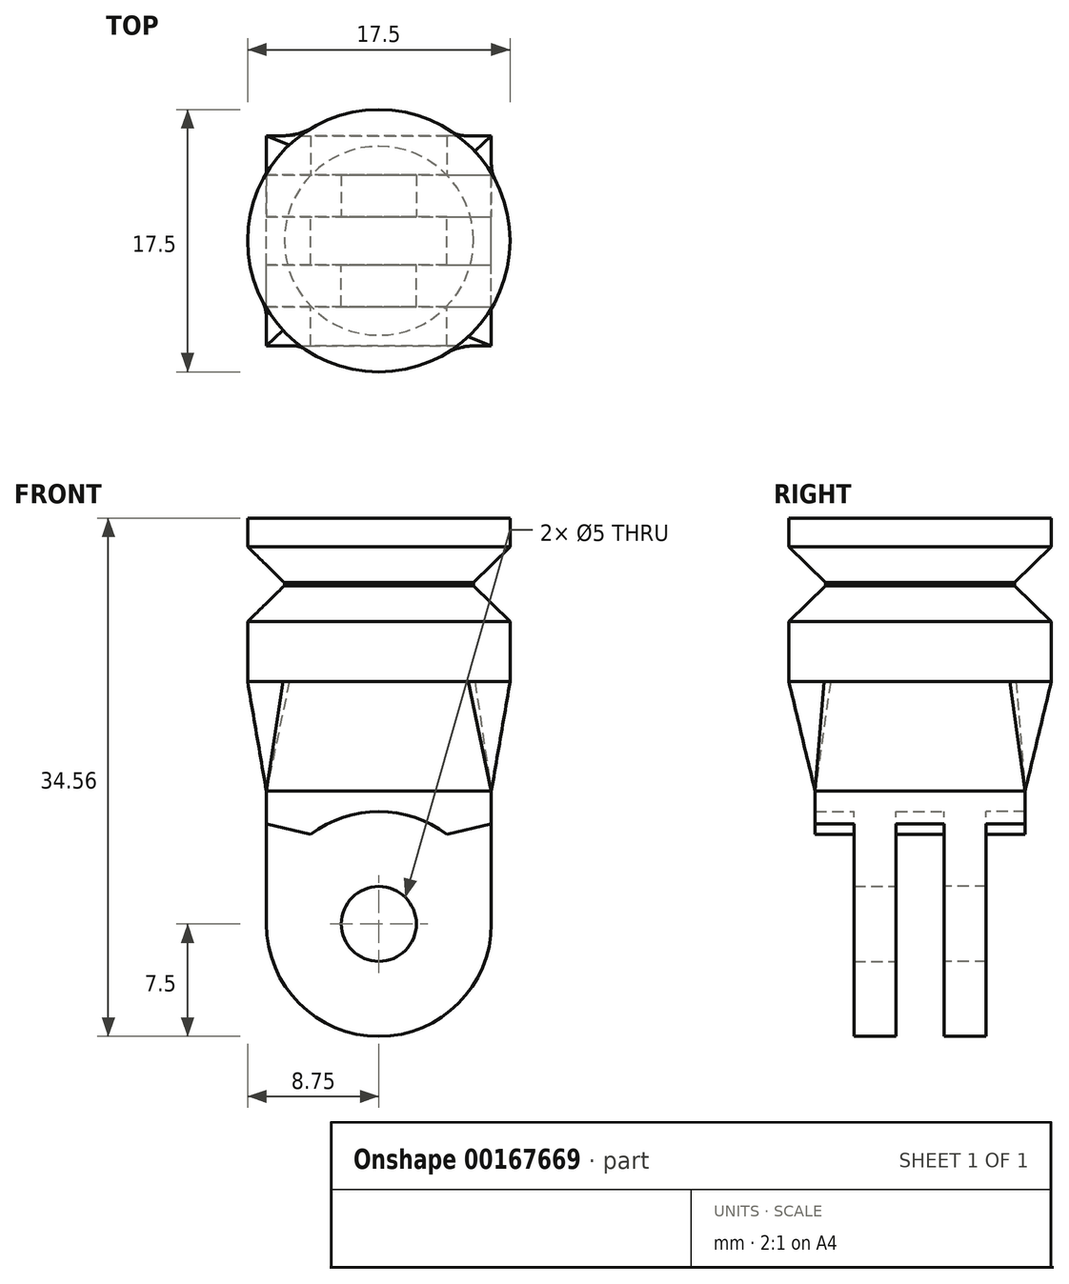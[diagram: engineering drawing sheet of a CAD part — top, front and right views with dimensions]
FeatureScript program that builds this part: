
annotation { "Feature Type Name" : "Feature", "Feature Type Description" : "" }
export const myFeature = defineFeature(function(context is Context, id is Id, definition is map)
    precondition{}
    {
        {
            var Q0;
            Q0=qCreatedBy(makeId("Front.planeOp"),FACE);
            var sketch = newSketch(context, id + "F0", { "sketchPlane" : qUnion([Q0])});
            skCircle(sketch, "E0", {"center": v(0, 0) * mm, "radius": 7.5 * mm});
            skCircle(sketch, "E1", {"center": v(0, 0) * mm, "radius": 2.5 * mm});
            skLineSegment(sketch, "E2", {"start": v(-7.5, 8.87) * mm, "end": v(-7.5, 0) * mm});
            skLineSegment(sketch, "E3", {"start": v(-7.5, 8.87) * mm, "end": v(7.5, 8.87) * mm});
            skLineSegment(sketch, "E4", {"start": v(7.5, 0) * mm, "end": v(7.5, 8.87) * mm});
            skLineSegment(sketch, "E5", {"start": v(-7.5, 6.68) * mm, "end": v(-4.54, 5.97) * mm});
            skLineSegment(sketch, "E6", {"start": v(0, 8.87) * mm, "end": v(0, -7.5) * mm});
            skLineSegment(sketch, "E7.MirrorCS", {"start": v(7.5, 6.68) * mm, "end": v(4.54, 5.97) * mm});
            skLineSegment(sketch, "E8", {"start": v(0, 27.06) * mm, "end": v(-8.75, 27.06) * mm});
            skLineSegment(sketch, "E9", {"start": v(-8.75, 27.06) * mm, "end": v(-8.75, 25.16) * mm});
            skLineSegment(sketch, "E10", {"start": v(-8.75, 25.16) * mm, "end": v(-6.3, 22.76) * mm});
            skLineSegment(sketch, "E11", {"start": v(-6.3, 22.76) * mm, "end": v(-6.3, 22.56) * mm});
            skLineSegment(sketch, "E12", {"start": v(-6.3, 22.56) * mm, "end": v(-8.75, 20.16) * mm});
            skLineSegment(sketch, "E13", {"start": v(-8.75, 20.16) * mm, "end": v(-8.75, 16.16) * mm});
            skLineSegment(sketch, "E14", {"start": v(-8.75, 25.16) * mm, "end": v(-8.75, 20.16) * mm, "construction": true});
            skLineSegment(sketch, "E15", {"start": v(-6.3, 22.66) * mm, "end": v(-8.75, 22.66) * mm, "construction": true});
            skLineSegment(sketch, "E16", {"start": v(0, 8.87) * mm, "end": v(0, 42.53) * mm});
            skLineSegment(sketch, "E17", {"start": v(-8.75, 16.16) * mm, "end": v(0, 16.16) * mm});
            skSolve(sketch);
        }
        {
            var Q0;
            {var subQ3=sQuery(id+"F0.wireOp",EDGE,"E7.MirrorCS");Q0=makeQuery(id+"F0.imprint","IMPRINT",FACE,{"disambiguationData":[TD([[makeQuery(id+"F0.imprint","IMPRINT",EDGE,{"derivedFrom":subQ3}),1.0]])]});}
            var Q1;
            {var subQ3=sQuery(id+"F0.wireOp",EDGE,"E5");Q1=makeQuery(id+"F0.imprint","IMPRINT",FACE,{"disambiguationData":[TD([[makeQuery(id+"F0.imprint","IMPRINT",EDGE,{"derivedFrom":subQ3}),-1.0]])]});}
            var Q2;
            {var subQ7=sQuery(id+"F0.wireOp",EDGE,"E7.MirrorCS");Q2=makeQuery(id+"F0.imprint","IMPRINT",FACE,{"disambiguationData":[TD([[makeQuery(id+"F0.imprint","IMPRINT",EDGE,{"derivedFrom":subQ7}),-1.0]])]});}
            var Q3;
            {var subQ0=sQuery(id+"F0.wireOp",EDGE,"E5");Q3=makeQuery(id+"F0.imprint","IMPRINT",FACE,{"disambiguationData":[TD([[makeQuery(id+"F0.imprint","IMPRINT",EDGE,{"derivedFrom":subQ0}),1.0]])]});}
            var Q4;
            {var subQ4=sQuery(id+"F0.wireOp",EDGE,"E0");var subQ6=makeQuery(id+"F0.imprint","INTERSECT",VERTEX,{"derivedFrom":[subQ4,sQuery(id+"F0.wireOp",EDGE,"E4")]});Q4=makeQuery(id+"F0.imprint","IMPRINT",FACE,{"disambiguationData":[TD([[makeQuery(id+"F0.imprint","IMPRINT",EDGE,{"disambiguationData":[TD([[subQ6,-1.0]])],"derivedFrom":subQ4}),1.0]])]});}
            var Q5;
            {var subQ4=sQuery(id+"F0.wireOp",EDGE,"E0");var subQ7=makeQuery(id+"F0.imprint","INTERSECT",VERTEX,{"derivedFrom":[subQ4,sQuery(id+"F0.wireOp",EDGE,"E5")]});Q5=makeQuery(id+"F0.imprint","IMPRINT",FACE,{"disambiguationData":[TD([[makeQuery(id+"F0.imprint","IMPRINT",EDGE,{"disambiguationData":[TD([[subQ7,1.0]])],"derivedFrom":subQ4}),1.0]])]});}
            extrude(context, id + "F1", {"entities" : qUnion([Q0, Q1, Q2, Q3, Q4, Q5]), "depth" : (3 + 3 / 2 - 0.1) * mm, "hasSecondDirection" : true, "secondDirectionOppositeDirection" : false, "secondDirectionDepth" : (3 / 2 + 0.1) * mm});
        }
        {
            var Q0;
            {var subQ0=sQuery(id+"F0.wireOp",EDGE,"E5");Q0=makeQuery(id+"F0.imprint","IMPRINT",FACE,{"disambiguationData":[TD([[makeQuery(id+"F0.imprint","IMPRINT",EDGE,{"derivedFrom":subQ0}),1.0]])]});}
            var Q1;
            {var subQ7=sQuery(id+"F0.wireOp",EDGE,"E7.MirrorCS");Q1=makeQuery(id+"F0.imprint","IMPRINT",FACE,{"disambiguationData":[TD([[makeQuery(id+"F0.imprint","IMPRINT",EDGE,{"derivedFrom":subQ7}),-1.0]])]});}
            extrude(context, id + "F2", {"entities" : qUnion([Q0, Q1]), "operationType" : NewBodyOperationType.ADD, "depth" : (3 + 3 / 2 + 5 / 2) * mm});
        }
        {
            var Q0;
            Q0=makeQuery(id+"F1.opExtrude","SWEPT_BODY",BODY,{"disambiguationData":[OSD([sQuery(id+"F0.wireOp",EDGE,"E0"),sQuery(id+"F0.wireOp",EDGE,"E1"),sQuery(id+"F0.wireOp",EDGE,"E2"),sQuery(id+"F0.wireOp",EDGE,"E3"),sQuery(id+"F0.wireOp",EDGE,"E4")])]});
            var Q1;
            Q1=makeQuery(id+"F2.opExtrude","CAP_FACE",FACE,{"disambiguationData":[OSD([sQuery(id+"F0.wireOp",EDGE,"E0"),sQuery(id+"F0.wireOp",EDGE,"E2"),sQuery(id+"F0.wireOp",EDGE,"E3"),sQuery(id+"F0.wireOp",EDGE,"E4"),sQuery(id+"F0.wireOp",EDGE,"E5"),sQuery(id+"F0.wireOp",EDGE,"E7.MirrorCS")])],"isStart":true});
            mirror(context, id + "F3", {"operationType" : NewBodyOperationType.ADD, "entities" : qUnion([Q0]), "mirrorPlane" : qUnion([Q1])});
        }
        {
            var Q0;
            {var subQ0=sQuery(id+"F0.wireOp",EDGE,"E8");Q0=makeQuery(id+"F0.imprint","IMPRINT",FACE,{"disambiguationData":[TD([[makeQuery(id+"F0.imprint","IMPRINT",EDGE,{"derivedFrom":subQ0}),1.0]])]});}
            var Q1;
            Q1=sQuery(id+"F0.wireOp",EDGE,"E16");
            revolve(context, id + "F4", {"entities" : qUnion([Q0]), "axis" : qUnion([Q1]), "revolveType" : RevolveType.FULL});
        }
        {
            var Q1;
            Q1=makeQuery(id+"F4.opRevolve","SWEPT_FACE",FACE,{"disambiguationData":[OSD([sQuery(id+"F0.wireOp",EDGE,"E17")])]});
            var Q2;
            {var subQ0=sQuery(id+"F0.wireOp",EDGE,"E3");var subQ1=makeQuery(id+"F2.boolean.opBoolean","MERGE",FACE,{"derivedFrom":[makeQuery(id+"F1.opExtrude","SWEPT_FACE",FACE,{"disambiguationData":[OSD([subQ0])]}),makeQuery(id+"F2.opExtrude","SWEPT_FACE",FACE,{"disambiguationData":[OSD([subQ0])]})]});Q2=makeQuery(id+"F3.boolean.opBoolean","MERGE",FACE,{"derivedFrom":[subQ1,makeQuery(id+"F3.opPattern","COPY",FACE,{"derivedFrom":subQ1,"instanceName":"1"})]});}
            loft(context, id + "F5", {"operationType" : NewBodyOperationType.ADD, "sheetProfilesArray" : [{ "sheetProfileEntities" : qUnion([Q1]) }, { "sheetProfileEntities" : qUnion([Q2]) }]});
        }
    });
